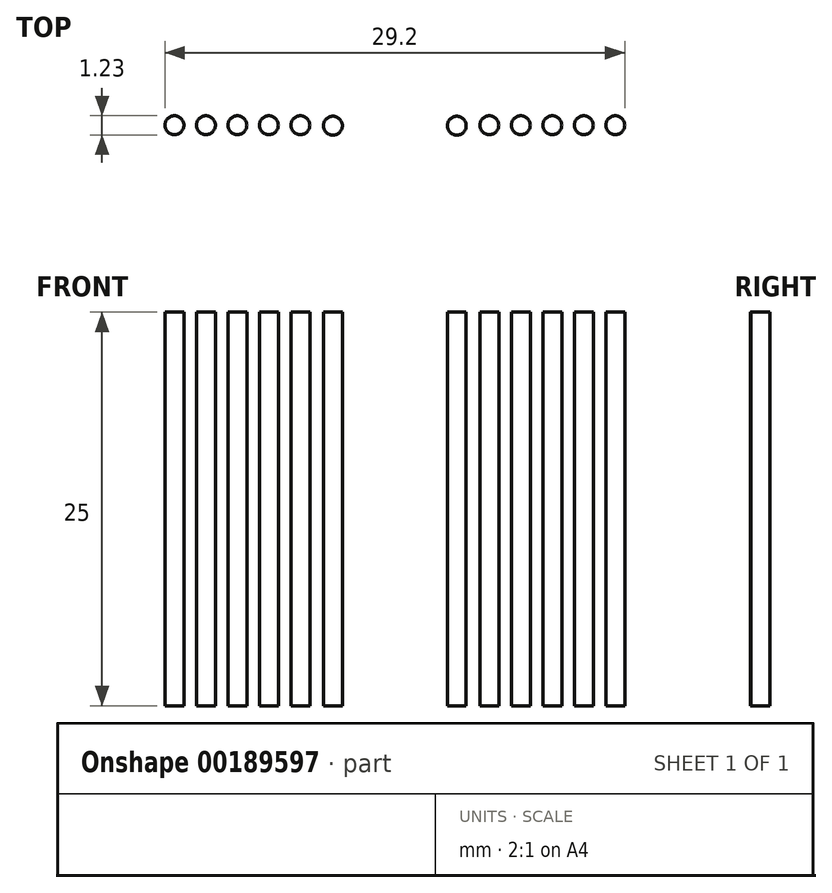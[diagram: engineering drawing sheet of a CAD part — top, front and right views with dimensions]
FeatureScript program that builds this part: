
annotation { "Feature Type Name" : "Feature", "Feature Type Description" : "" }
export const myFeature = defineFeature(function(context is Context, id is Id, definition is map)
    precondition{}
    {
        {
            var Q0;
            Q0=qCreatedBy(makeId("Top.planeOp"),FACE);
            var sketch = newSketch(context, id + "F0", { "sketchPlane" : qUnion([Q0])});
            skArc(sketch, "E0", {"start": v(2.23, 2.5) * mm, "mid": v(0, 3.35) * mm, "end": v(-2.23, 2.5) * mm});
            skCircle(sketch, "E1", {"center": v(6, 0) * mm, "radius": 0.6 * mm});
            skCircle(sketch, "E2.1.0.0", {"center": v(8, 0) * mm, "radius": 0.6 * mm});
            skCircle(sketch, "E2.2.0.0", {"center": v(10, 0) * mm, "radius": 0.6 * mm});
            skCircle(sketch, "E2.3.0.0", {"center": v(12, 0) * mm, "radius": 0.6 * mm});
            skCircle(sketch, "E2.4.0.0", {"center": v(14, 0) * mm, "radius": 0.6 * mm});
            skLineSegment(sketch, "E3", {"start": v(0, 0) * mm, "end": v(18.4, 0) * mm, "construction": true});
            skCircle(sketch, "E4", {"center": v(3.93, -0.03) * mm, "radius": 0.6 * mm});
            skLineSegment(sketch, "E5", {"start": v(2.23, 2.5) * mm, "end": v(13.99, 1.95) * mm});
            skLineSegment(sketch, "E6", {"start": v(2.23, 2.5) * mm, "end": v(2.23, 2.5) * mm});
            skLineSegment(sketch, "E7.MirrorCS", {"start": v(2.23, -2.5) * mm, "end": v(13.99, -1.95) * mm});
            skArc(sketch, "E8", {"start": v(14, -1.95) * mm, "mid": v(15.95, 0) * mm, "end": v(14, 1.95) * mm});
            skLineSegment(sketch, "E9", {"start": v(0, 0) * mm, "end": v(0, 7.53) * mm, "construction": true});
            skLineSegment(sketch, "E10.MirrorCS", {"start": v(-2.23, 2.5) * mm, "end": v(-13.99, 1.95) * mm});
            skArc(sketch, "E11.MirrorCS", {"start": v(-14, -1.95) * mm, "mid": v(-15.95, 0) * mm, "end": v(-14, 1.95) * mm});
            skCircle(sketch, "E12.MirrorC", {"center": v(-14, 0) * mm, "radius": 0.6 * mm});
            skCircle(sketch, "E13.MirrorC", {"center": v(-12, 0) * mm, "radius": 0.6 * mm});
            skCircle(sketch, "E14.MirrorC", {"center": v(-10, 0) * mm, "radius": 0.6 * mm});
            skCircle(sketch, "E15.MirrorC", {"center": v(-8, 0) * mm, "radius": 0.6 * mm});
            skCircle(sketch, "E16.MirrorC", {"center": v(-6, 0) * mm, "radius": 0.6 * mm});
            skCircle(sketch, "E17.MirrorC", {"center": v(-3.93, -0.03) * mm, "radius": 0.6 * mm});
            skLineSegment(sketch, "E18.MirrorCS", {"start": v(-2.23, -2.5) * mm, "end": v(-13.99, -1.95) * mm});
            skArc(sketch, "E19.trimOffspring", {"start": v(-2.23, -2.5) * mm, "mid": v(0, -3.35) * mm, "end": v(2.23, -2.5) * mm});
            skSolve(sketch);
        }
        {
            var Q0;
            Q0 = qSketchRegion(id + "F0", true);
            extrude(context, id + "F1", {"entities" : qUnion([Q0]), "depth" : 25 * mm});
        }
    });
